# Revit family: 6228.04-EPIC BLOC 3 PC WALL TOP ASSEMBLY
name_source: partatom
category: Plumbing Fixtures
revit_build: Autodesk Revit 2015 (Build: 20140606_1530(x64)
units: mm (PartAtom-declared; Revit-internal decimal feet)

## types (6) — shared parameters
Assembly Code = D2020300
CW Connection = Yes
HW Connection = Yes
Manufacturer = GWA Bathrooms & Kitchens
Type Comments = EPIC BLOC 3 PC WALL TOP ASSEMBLY
URL = https://www.dorf.com.au
Vent Connection = No
WELSRating_ANZRS = 0
Waste Connection = No
zero-valued in all types: Default Elevation

## per-type parameters (varying)
| type | Material_ANZRS | Material_Handle | Model |
| Chrome | GWA_Metal-Chrome | GWA_Metal-Chrome | 6228.04 |
| Black | GWA-Metal-Black | GWA-Metal-Black | 6218.09 |
| Chrome with Black Handle | GWA_Metal-Chrome | GWA-Metal-Black | 6218.49 |
| Black with Gold Handle | GWA-Metal-Black | GWA-Metal-Gold | 6218.92 |
| Black with Copper Handle | GWA-Metal-Black | GWA-Metal-Copper | 6218.94 |
| Black with RoseGold Handle | GWA-Metal-Black | GWA-Metal-RoseGold | 6218.93 |

## geometry (parser evidence)
native form markers: Sweep x5
no freeform markers — native parametric forms only
